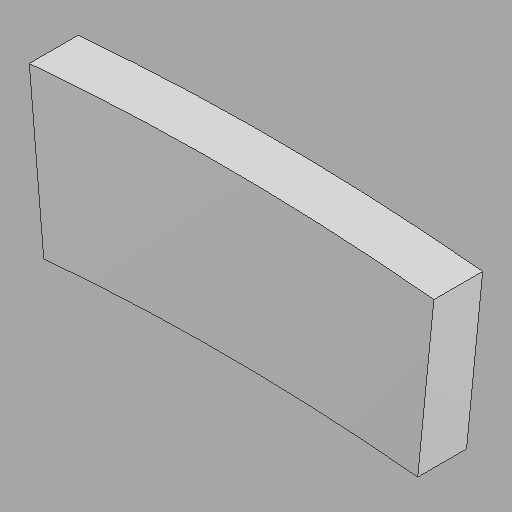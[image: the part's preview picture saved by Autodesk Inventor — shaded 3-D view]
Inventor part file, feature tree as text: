
AUTODESK INVENTOR PART (.ipt)
format: ipt  version: 2022.1 (Build 261234020, 234B)  size: 89,088 bytes
history: imported  units: in
note: dims shown in document units (in); Inventor stores cm internally (conversion verified against a paired STEP export)
features: imported_body x1
ambient origin geometry x8: Origin, YZ Plane, XZ Plane, XY Plane, X Axis, Y Axis, Z Axis, Center Point
bodies: Solid1 (imported_parasolid)
feature tree (1):
  imported_body  NMx_Import_Brep_tag  [imported B-rep: ~6 faces, bbox_mm=[1263.659676, 512.295091, 152.4]]
